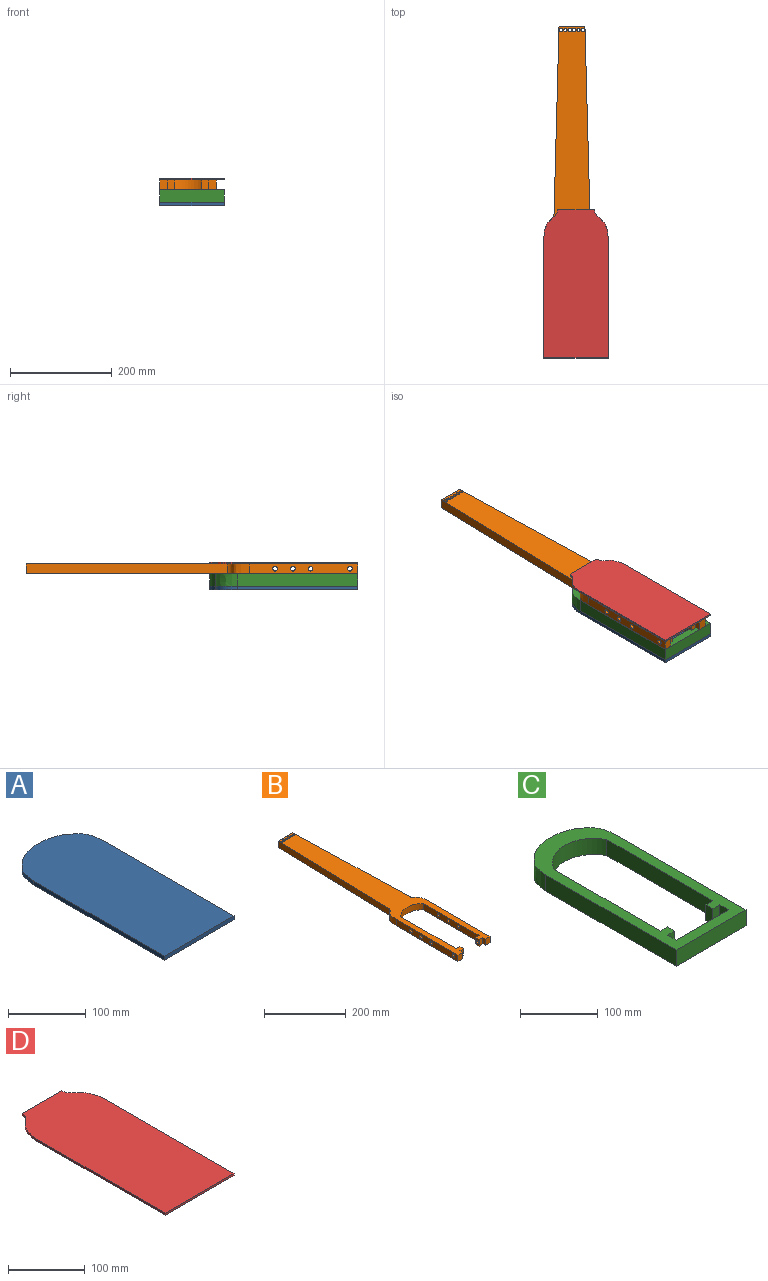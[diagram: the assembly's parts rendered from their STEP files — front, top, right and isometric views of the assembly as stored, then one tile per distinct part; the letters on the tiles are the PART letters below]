
ASSEMBLY  parts=4 mates=9
PART A: 8 faces, bbox 127x292.1x6.4 mm
  f0: plane 237.47x6.35mm, normal (1,0,0), area 1507.9mm2, adj f2,f3,f4,f7
  f1: plane 237.34x6.35mm, normal (-1,0,0), area 1507.1mm2, adj f2,f3,f4,f5
  f2: plane 127x6.35mm, normal (0,-1,0), area 806.5mm2, adj f0,f1,f3,f4
  f3: plane 292.1x127.01mm, normal (0,0,-1), area 35693.5mm2, adj f0,f1,f2,f5,f6,f7
  f4: plane 292.1x127.01mm, normal (0,0,1), area 35693.5mm2, adj f0,f1,f2,f5,f6,f7
  f5: extruded ~43.4x22.77mm, area 324.5mm2, adj f1,f3,f4,f6
  f6: cylinder r=78.71mm len=81.48mm, axis (0,0,1), area 543.8mm2, adj f3,f4,f5,f7
  f7: extruded ~43.27x22.76mm, area 323.7mm2, adj f0,f3,f4,f6
PART B: 36 faces, bbox 111.1x654.1x19.1 mm
  f0: plane 19.05x15.88mm, normal (0,-1,0), area 302.4mm2, adj f2,f3,f5,f14
  f1: plane 214.14x19.05mm, normal (1,0,0), area 3825.4mm2, adj f2,f3,f6,f21,f28,f29,f30,f31
  f2: plane 654.05x111.13mm, normal (0,0,1), area 34710.4mm2, adj f0,f1,f4,f5,f6,f7,f8,f9
  f3: plane 654.05x111.13mm, normal (0,0,-1), area 34710.4mm2, adj f0,f1,f4,f5,f6,f7,f8,f9
  f4: plane 51.07x19.05mm, normal (0,1,0), area 972.9mm2, adj f2,f3,f7,f8
  f5: plane 214.06x19.05mm, normal (-1,0,0), area 3823.8mm2, adj f0,f2,f3,f9,f32,f33,f34,f35
  f6: plane 19.05x15.87mm, normal (0,-1,0), area 302.3mm2, adj f1,f2,f3,f15
  f7: plane 396.88x19.05mm, normal (1,0.03,0), area 7563.2mm2, adj f2,f3,f4,f21
  f8: plane 396.88x19.05mm, normal (-1,0.03,0), area 7563.2mm2, adj f2,f3,f4,f9
  f9: extruded ~43.12x19.45mm, area 948.7mm2, adj f2,f3,f5,f8
  f10: plane 191.83x19.05mm, normal (1,0,0), area 3463.9mm2, adj f2,f3,f11,f20,f33,f34,f35
  f11: plane 19.05x12.7mm, normal (0,1,0), area 241.9mm2, adj f2,f3,f10,f12
  f12: plane 19.05x12.7mm, normal (1,0,0), area 178.4mm2, adj f2,f3,f11,f13,f32
  f13: plane 19.05x12.7mm, normal (0,-1,0), area 241.9mm2, adj f2,f3,f12,f14
  f14: plane 19.05x9.53mm, normal (1,0,0), area 181.5mm2, adj f0,f2,f3,f13
  f15: plane 19.05x9.53mm, normal (-1,0,0), area 181.5mm2, adj f2,f3,f6,f16
  f16: plane 19.05x12.7mm, normal (0,-1,0), area 241.9mm2, adj f2,f3,f15,f17
  f17: plane 19.05x12.7mm, normal (-1,0,0), area 178.4mm2, adj f2,f3,f16,f18,f31
  f18: plane 19.05x12.7mm, normal (0,1,0), area 241.9mm2, adj f2,f3,f17,f19
  f19: plane 191.83x19.05mm, normal (-1,0,0), area 3463.8mm2, adj f2,f3,f18,f20,f28,f29,f30
  f20: cylinder r=53.31mm len=79.38mm, axis (0,0,1), area 1705.7mm2, adj f2,f3,f10,f19
  f21: extruded ~43.03x19.45mm, area 947.1mm2, adj f1,f2,f3,f7
  f22: cylinder r=3.25mm len=19.05mm, axis (0,0,1), area 389.2mm2, adj f2,f3
  f23: cylinder r=3.25mm len=19.05mm, axis (0,0,1), area 389.2mm2, adj f2,f3
  f24: cylinder r=3.25mm len=19.05mm, axis (0,0,1), area 389.2mm2, adj f2,f3
  f25: cylinder r=3.25mm len=19.05mm, axis (0,0,1), area 389.2mm2, adj f2,f3
  f26: cylinder r=3.25mm len=19.05mm, axis (0,0,1), area 389.2mm2, adj f2,f3
  f27: cylinder r=3.25mm len=19.05mm, axis (0,0,1), area 389.2mm2, adj f2,f3
  f28: cylinder r=4.5mm len=15.87mm, axis (-1,0,0), area 448.3mm2, adj f1,f19
  f29: cylinder r=4.5mm len=15.87mm, axis (-1,0,0), area 448.3mm2, adj f1,f19
  f30: cylinder r=4.5mm len=15.87mm, axis (-1,0,0), area 448.3mm2, adj f1,f19
  f31: cylinder r=4.5mm len=28.57mm, axis (-1,0,0), area 807.1mm2, adj f1,f17
  f32: cylinder r=4.5mm len=28.58mm, axis (-1,0,0), area 807.2mm2, adj f5,f12
  f33: cylinder r=4.5mm len=15.88mm, axis (-1,0,0), area 448.4mm2, adj f5,f10
  f34: cylinder r=4.5mm len=15.88mm, axis (-1,0,0), area 448.4mm2, adj f5,f10
  f35: cylinder r=4.5mm len=15.88mm, axis (-1,0,0), area 448.4mm2, adj f5,f10
PART C: 20 faces, bbox 127x292.1x25.4 mm
  f0: plane 237.47x25.4mm, normal (1,0,0), area 6031.6mm2, adj f1,f2,f4,f7
  f1: plane 292.1x127.01mm, normal (0,0,1), area 12920.8mm2, adj f0,f3,f4,f5,f6,f7,f8,f9
  f2: plane 292.1x127.01mm, normal (0,0,-1), area 12920.8mm2, adj f0,f3,f4,f5,f6,f7,f8,f9
  f3: plane 237.34x25.4mm, normal (-1,0,0), area 6028.5mm2, adj f1,f2,f4,f5
  f4: plane 127x25.4mm, normal (0,-1,0), area 3225.8mm2, adj f0,f1,f2,f3
  f5: extruded ~43.4x25.4mm, area 1298mm2, adj f1,f2,f3,f6
  f6: cylinder r=78.71mm len=81.48mm, axis (0,0,1), area 2175.2mm2, adj f1,f2,f5,f7
  f7: extruded ~43.27x25.4mm, area 1294.7mm2, adj f0,f1,f2,f6
  f8: plane 192.89x25.4mm, normal (1,0,0), area 4899.5mm2, adj f1,f2,f9,f19
  f9: plane 25.4x12.7mm, normal (0,1,0), area 322.6mm2, adj f1,f2,f8,f10
  f10: plane 25.4x12.7mm, normal (1,0,0), area 322.6mm2, adj f1,f2,f9,f11
  f11: plane 25.4x12.7mm, normal (0,-1,0), area 322.6mm2, adj f1,f2,f10,f12
  f12: plane 25.4x15.88mm, normal (1,0,0), area 403.2mm2, adj f1,f2,f11,f13
  f13: plane 95.26x25.4mm, normal (0,1,0), area 2419.5mm2, adj f1,f2,f12,f14
  f14: plane 25.4x15.88mm, normal (-1,0,0), area 403.2mm2, adj f1,f2,f13,f15
  f15: plane 25.4x12.7mm, normal (0,-1,0), area 322.6mm2, adj f1,f2,f14,f16
  f16: plane 25.4x12.7mm, normal (-1,0,0), area 322.6mm2, adj f1,f2,f15,f17
  f17: plane 25.4x12.7mm, normal (0,1,0), area 322.6mm2, adj f1,f2,f16,f18
  f18: plane 192.88x25.4mm, normal (-1,0,0), area 4899.2mm2, adj f1,f2,f17,f19
  f19: cylinder r=53.31mm len=95.26mm, axis (0,0,1), area 2992.3mm2, adj f1,f2,f8,f18
PART D: 10 faces, bbox 127x292.1x3.2 mm
  f0: plane 237.47x3.18mm, normal (1,0,0), area 754mm2, adj f1,f3,f4,f8
  f1: plane 292.1x127.01mm, normal (0,0,-1), area 35925.1mm2, adj f0,f2,f3,f5,f6,f7,f8,f9
  f2: plane 237.34x3.18mm, normal (-1,0,0), area 753.6mm2, adj f1,f3,f4,f5
  f3: plane 127x3.18mm, normal (0,-1,0), area 403.2mm2, adj f0,f1,f2,f4
  f4: plane 292.1x127.01mm, normal (0,0,1), area 35925.1mm2, adj f0,f2,f3,f5,f6,f7,f8,f9
  f5: extruded ~43.4x22.77mm, area 162.3mm2, adj f1,f2,f4,f9
  f6: plane 72.33x3.18mm, normal (0,1,0), area 229.7mm2, adj f1,f4,f7,f9
  f7: extruded ~11.37x4.58mm, area 39.5mm2, adj f1,f4,f6,f8
  f8: extruded ~43.27x22.76mm, area 161.8mm2, adj f0,f1,f4,f7
  f9: extruded ~11.36x4.57mm, area 39.5mm2, adj f1,f4,f5,f6
PLACE A t=(34.92,-9.52,-25.4)mm
PLACE B t=(26.99,-9.52,19.05)mm
PLACE C t=(34.93,-9.52,0)mm
PLACE D t=(34.93,-9.52,22.23)mm
MATE planar C.f1 <-> B.f20  axis (0,0,1) through (34.92,135,0)mm
MATE planar B.f0 <-> C.f4  axis (0,-1,0) through (-20.64,-9.52,9.53)mm
MATE planar D.f2 <-> B.f5  axis (-1,0,0) through (-28.57,109.15,20.64)mm
MATE planar A.f2 <-> C.f4  axis (0,-1,0) through (34.93,-9.52,-28.58)mm
MATE planar D.f3 <-> C.f4  axis (0,-1,0) through (34.93,-9.52,20.64)mm
MATE planar B.f2 <-> D.f1  axis (0,0,1) through (26.99,343.82,19.05)mm
MATE planar C.f3 <-> B.f5  axis (-1,0,0) through (-28.57,109.15,-12.7)mm
MATE planar A.f1 <-> C.f3  axis (-1,0,0) through (-28.58,109.15,-28.58)mm
MATE planar A.f4 <-> C.f2  axis (0,0,1) through (34.93,131.25,-25.4)mm
